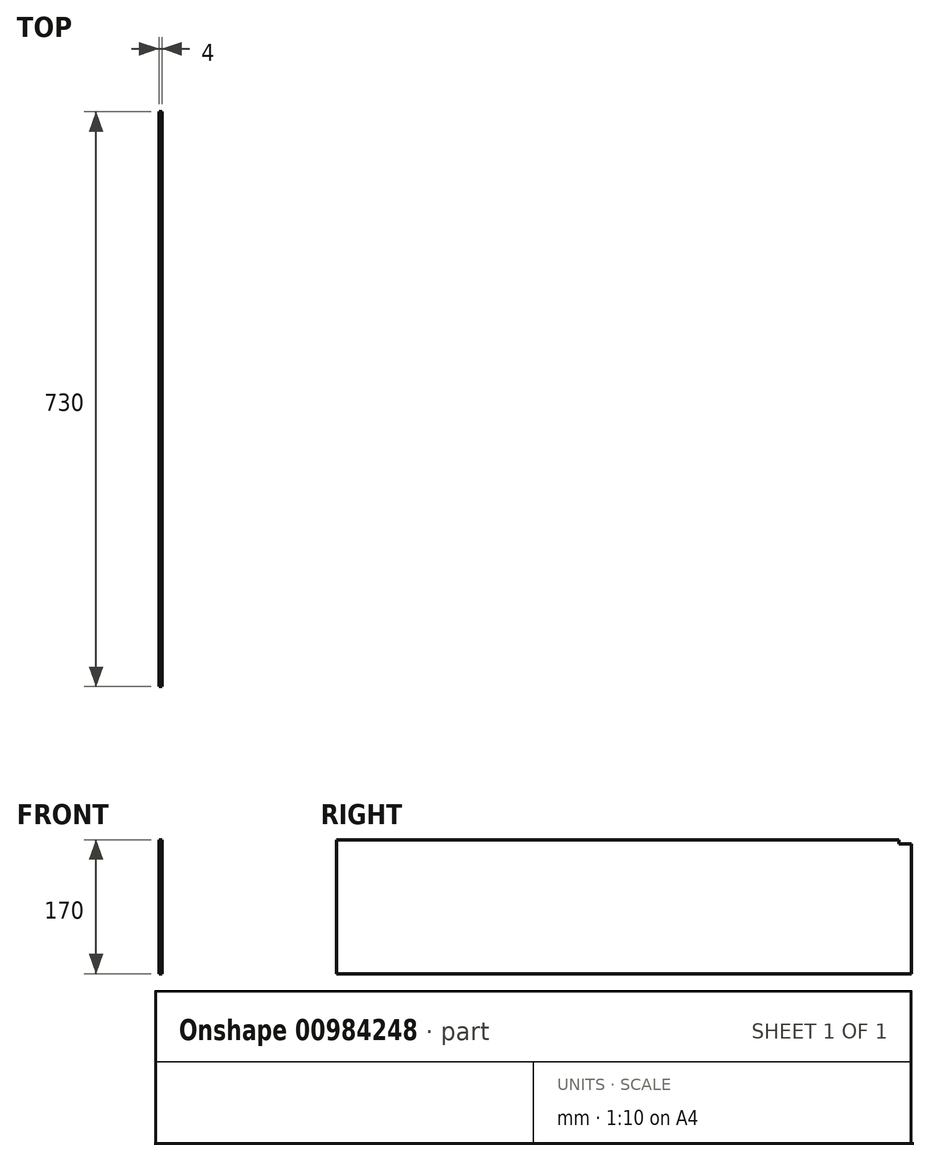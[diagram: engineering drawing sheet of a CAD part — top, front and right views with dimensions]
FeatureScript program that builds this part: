
annotation { "Feature Type Name" : "Feature", "Feature Type Description" : "" }
export const myFeature = defineFeature(function(context is Context, id is Id, definition is map)
    precondition{}
    {
        {
            var Q0;
            Q0=qCreatedBy(makeId("Front.planeOp"),FACE);
            var sketch = newSketch(context, id + "F0", { "sketchPlane" : qUnion([Q0])});
            skLineSegment(sketch, "E0.bottom", {"start": v(2, 85) * mm, "end": v(-2, 85) * mm});
            skLineSegment(sketch, "E0.top", {"start": v(2, -85) * mm, "end": v(-2, -85) * mm});
            skLineSegment(sketch, "E0.left", {"start": v(2, 85) * mm, "end": v(2, -85) * mm});
            skLineSegment(sketch, "E0.right", {"start": v(-2, 85) * mm, "end": v(-2, -85) * mm});
            skPoint(sketch, "E0.middle", {"position": v(0, 0) * mm});
            skSolve(sketch);
        }
        {
            var Q0;
            Q0=makeQuery(id+"F0.imprint","IMPRINT",FACE,{"disambiguationData":[TD([[makeQuery(id+"F0.imprint","IMPRINT",EDGE,{"derivedFrom":sQuery(id+"F0.wireOp",EDGE,"E0.bottom")}),1.0]])]});
            extrude(context, id + "F1", {"entities" : qUnion([Q0]), "depth" : 730 * mm, "offsetDistance" : 25 * mm});
        }
        {
            var Q0;
            Q0=makeQuery(id+"F1.opExtrude","SWEPT_FACE",FACE,{"disambiguationData":[OSD([sQuery(id+"F0.wireOp",EDGE,"E0.left")])]});
            var sketch = newSketch(context, id + "F2", { "sketchPlane" : qUnion([Q0])});
            skLineSegment(sketch, "E1.bottom", {"start": v(0, 85) * mm, "end": v(-16, 85) * mm});
            skLineSegment(sketch, "E1.top", {"start": v(0, 80) * mm, "end": v(-16, 80) * mm});
            skLineSegment(sketch, "E1.left", {"start": v(0, 85) * mm, "end": v(0, 80) * mm});
            skLineSegment(sketch, "E1.right", {"start": v(-16, 85) * mm, "end": v(-16, 80) * mm});
            skSolve(sketch);
        }
        {
            var Q0;
            Q0=makeQuery(id+"F2.imprint","IMPRINT",FACE,{"disambiguationData":[TD([[makeQuery(id+"F2.imprint","IMPRINT",EDGE,{"derivedFrom":sQuery(id+"F2.wireOp",EDGE,"E1.bottom")}),-1.0]])]});
            extrude(context, id + "F3", {"entities" : qUnion([Q0]), "operationType" : NewBodyOperationType.REMOVE, "oppositeDirection" : true, "depth" : 25 * mm, "offsetDistance" : 25 * mm});
        }
    });
